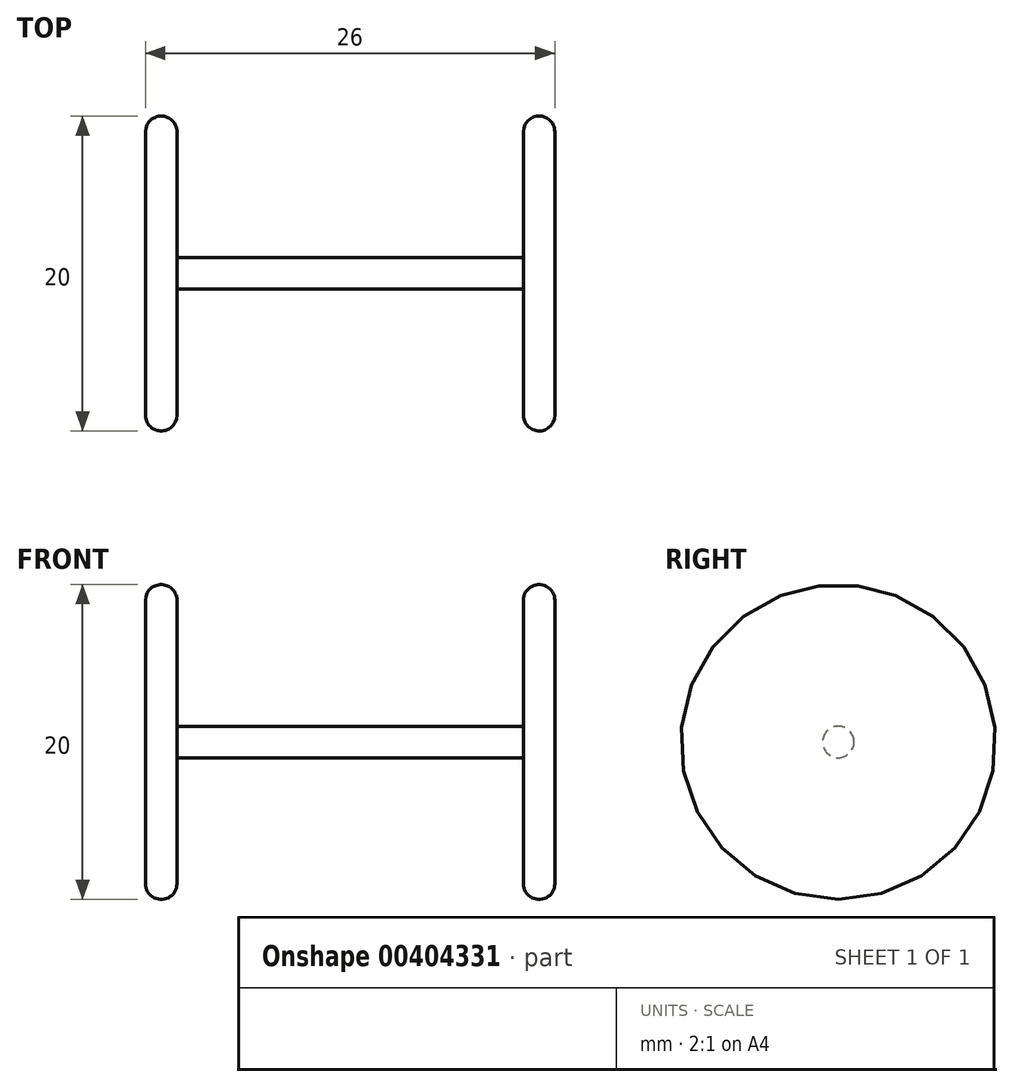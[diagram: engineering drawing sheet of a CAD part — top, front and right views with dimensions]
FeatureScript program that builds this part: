
annotation { "Feature Type Name" : "Feature", "Feature Type Description" : "" }
export const myFeature = defineFeature(function(context is Context, id is Id, definition is map)
    precondition{}
    {
        {
            var Q0;
            Q0=qCreatedBy(makeId("Right.planeOp"),FACE);
            var sketch = newSketch(context, id + "F0", { "sketchPlane" : qUnion([Q0])});
            skCircle(sketch, "E0", {"center": v(55.18, 16.73) * mm, "radius": 10 * mm});
            skSolve(sketch);
        }
        {
            var Q0;
            Q0 = qSketchRegion(id + "F0", true);
            extrude(context, id + "F1", {"entities" : qUnion([Q0]), "depth" : 2 * mm});
        }
        {
            var Q0;
            Q0=makeQuery(id+"F1.opExtrude","CAP_FACE",FACE,{"disambiguationData":[OSD([sQuery(id+"F0.wireOp",EDGE,"E0")])],"isStart":false});
            var sketch = newSketch(context, id + "F2", { "sketchPlane" : qUnion([Q0])});
            skCircle(sketch, "E1", {"center": v(55.18, 16.73) * mm, "radius": 1 * mm});
            skSolve(sketch);
        }
        {
            var Q0;
            Q0 = qSketchRegion(id + "F2", true);
            extrude(context, id + "F3", {"entities" : qUnion([Q0]), "operationType" : NewBodyOperationType.ADD, "depth" : 22 * mm});
        }
        {
            var Q0;
            Q0=makeQuery(id+"F3.opExtrude","CAP_FACE",FACE,{"disambiguationData":[OSD([sQuery(id+"F2.wireOp",EDGE,"E1")])],"isStart":false});
            var sketch = newSketch(context, id + "F4", { "sketchPlane" : qUnion([Q0])});
            skCircle(sketch, "E2", {"center": v(55.18, 16.73) * mm, "radius": 10 * mm});
            skSolve(sketch);
        }
        {
            var Q0;
            Q0 = qSketchRegion(id + "F4", true);
            extrude(context, id + "F5", {"entities" : qUnion([Q0]), "operationType" : NewBodyOperationType.ADD, "depth" : 2 * mm});
        }
        {
            var Q0;
            Q0=makeQuery(id+"F1.opExtrude","CAP_EDGE",EDGE,{"disambiguationData":[OSD([sQuery(id+"F0.wireOp",EDGE,"E0")])],"isStart":false});
            var Q1;
            Q1=makeQuery(id+"F1.opExtrude","CAP_EDGE",EDGE,{"disambiguationData":[OSD([sQuery(id+"F0.wireOp",EDGE,"E0")])],"isStart":true});
            var Q2;
            Q2=makeQuery(id+"F5.opExtrude","CAP_EDGE",EDGE,{"disambiguationData":[OSD([sQuery(id+"F4.wireOp",EDGE,"E2")])],"isStart":false});
            var Q3;
            Q3=makeQuery(id+"F5.opExtrude","CAP_EDGE",EDGE,{"disambiguationData":[OSD([sQuery(id+"F4.wireOp",EDGE,"E2")])],"isStart":true});
            fillet(context, id + "F6", {"entities" : qUnion([Q0, Q1, Q2, Q3]), "radius" : 1 * mm, "tangentPropagation" : true, "allowEdgeOverflow" : false});
        }
    });
